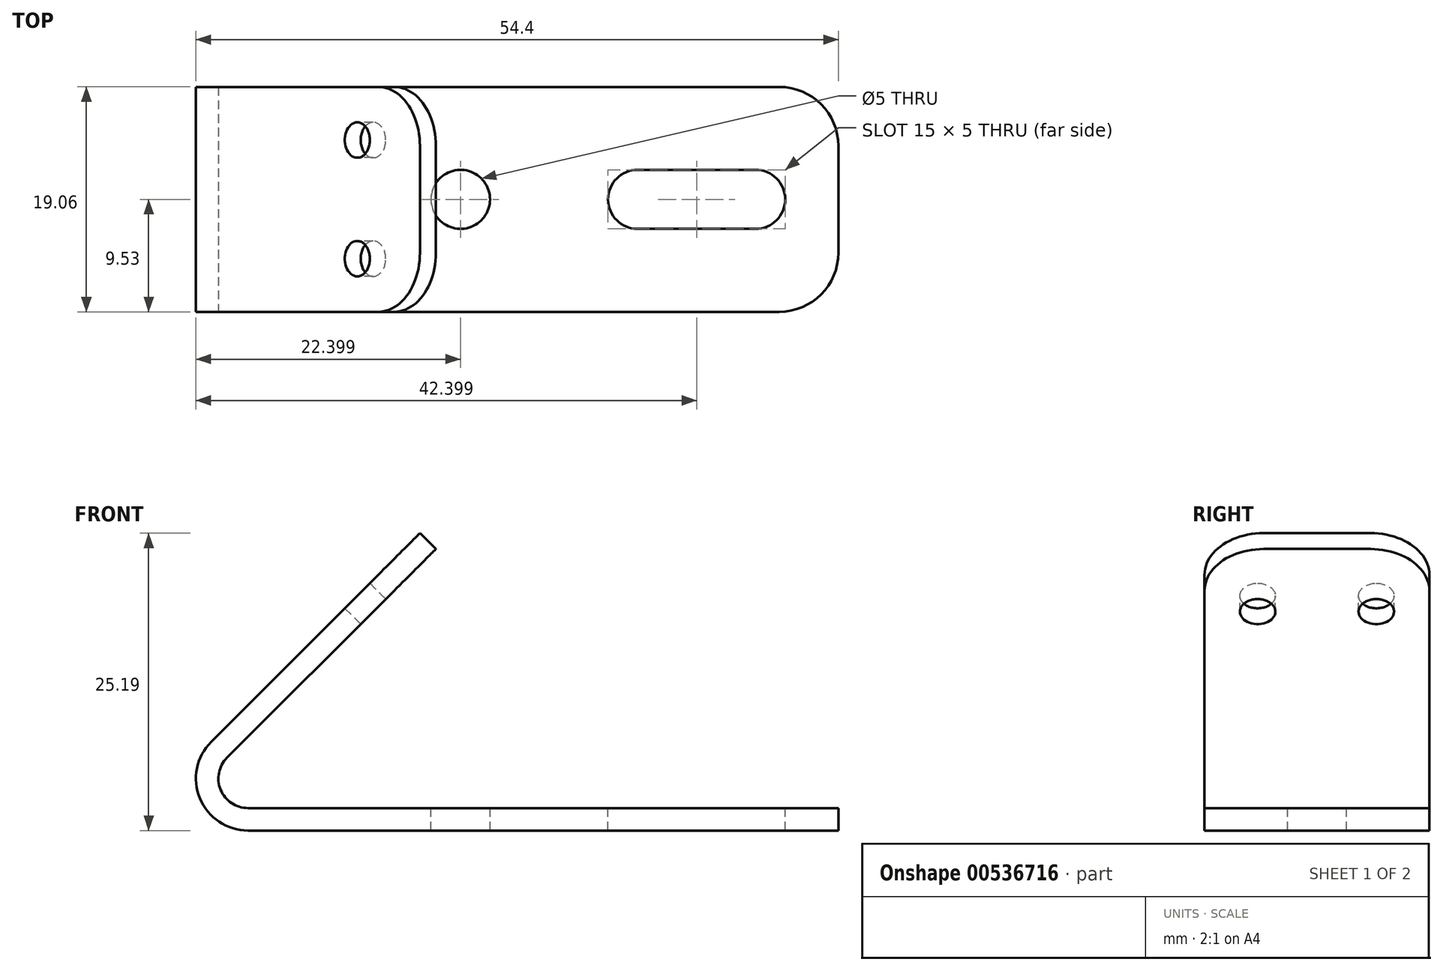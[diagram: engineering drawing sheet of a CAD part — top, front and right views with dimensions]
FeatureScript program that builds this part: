
annotation { "Feature Type Name" : "Feature", "Feature Type Description" : "" }
export const myFeature = defineFeature(function(context is Context, id is Id, definition is map)
    precondition{}
    {
        {
            var Q0;
            Q0=qCreatedBy(makeId("Front.planeOp"),FACE);
            var sketch = newSketch(context, id + "F0", { "sketchPlane" : qUnion([Q0])});
            skLineSegment(sketch, "E0", {"start": v(4.38, -27.35) * mm, "end": v(-45.62, -27.35) * mm});
            skLineSegment(sketch, "E1", {"start": v(-48.73, -19.84) * mm, "end": v(-31.06, -2.16) * mm});
            skLineSegment(sketch, "E2", {"start": v(-29.71, -3.5) * mm, "end": v(-47.39, -21.18) * mm});
            skLineSegment(sketch, "E3", {"start": v(-45.62, -25.45) * mm, "end": v(4.38, -25.45) * mm});
            skLineSegment(sketch, "E4", {"start": v(4.38, -25.45) * mm, "end": v(4.38, -27.35) * mm});
            skPoint(sketch, "E5.visualSharp", {"position": v(-56.24, -27.35) * mm});
            skArc(sketch, "E5.filletArc", {"start": v(-48.73, -19.84) * mm, "mid": v(-49.69, -24.63) * mm, "end": v(-45.62, -27.35) * mm});
            skLineSegment(sketch, "E6", {"start": v(-31.06, -2.16) * mm, "end": v(-29.71, -3.5) * mm});
            skPoint(sketch, "E7.visualSharp", {"position": v(-51.66, -25.45) * mm});
            skArc(sketch, "E7.filletArc", {"start": v(-47.39, -21.18) * mm, "mid": v(-47.93, -23.9) * mm, "end": v(-45.62, -25.45) * mm});
            skSolve(sketch);
        }
        {
            var Q0;
            Q0 = qSketchRegion(id + "F0", true);
            extrude(context, id + "F1", {"entities" : qUnion([Q0]), "endBound" : BoundingType.SYMMETRIC, "oppositeDirection" : true, "depth" : 19.05 * mm, "offsetDistance" : 25 * mm});
        }
        {
            var Q0;
            Q0=makeQuery(id+"F1.opExtrude","SWEPT_FACE",FACE,{"disambiguationData":[OSD([sQuery(id+"F0.wireOp",EDGE,"E1")])]});
            var sketch = newSketch(context, id + "F2", { "sketchPlane" : qUnion([Q0])});
            skLineSegment(sketch, "E8", {"start": v(-9.53, -23.49) * mm, "end": v(9.52, -23.49) * mm});
            skLineSegment(sketch, "E9", {"start": v(-9.53, -48.49) * mm, "end": v(-9.53, -23.49) * mm});
            skLineSegment(sketch, "E10", {"start": v(-9.53, -48.49) * mm, "end": v(9.52, -48.49) * mm});
            skLineSegment(sketch, "E11", {"start": v(9.53, -48.49) * mm, "end": v(9.53, -23.49) * mm});
            skCircle(sketch, "E12", {"center": v(-5.03, -30.99) * mm, "radius": 1.5 * mm});
            skCircle(sketch, "E13", {"center": v(5.03, -30.99) * mm, "radius": 1.5 * mm});
            skSolve(sketch);
        }
        {
            var Q0;
            Q0=makeQuery(id+"F2.imprint","IMPRINT",FACE,{"disambiguationData":[TD([[makeQuery(id+"F2.imprint","IMPRINT",EDGE,{"derivedFrom":sQuery(id+"F2.wireOp",EDGE,"E12")}),1.0]])]});
            var Q1;
            Q1=makeQuery(id+"F2.imprint","IMPRINT",FACE,{"disambiguationData":[TD([[makeQuery(id+"F2.imprint","IMPRINT",EDGE,{"derivedFrom":sQuery(id+"F2.wireOp",EDGE,"E13")}),1.0]])]});
            var Q2;
            Q2=sQuery(id+"F2.wireOp",EDGE,"E12");
            var Q3;
            Q3=sQuery(id+"F2.wireOp",EDGE,"E13");
            var Q4;
            Q4=makeQuery(id+"F1.opExtrude","SWEPT_FACE",FACE,{"disambiguationData":[OSD([sQuery(id+"F0.wireOp",EDGE,"E2")])]});
            extrude(context, id + "F3", {"entities" : qUnion([Q0, Q1]), "operationType" : NewBodyOperationType.REMOVE, "surfaceEntities" : qUnion([Q2, Q3]), "endBound" : BoundingType.UP_TO_SURFACE, "oppositeDirection" : true, "depth" : 25 * mm, "endBoundEntityFace" : qUnion([Q4]), "offsetDistance" : 25 * mm});
        }
        {
            var Q0;
            Q0=makeQuery(id+"F1.opExtrude","SWEPT_FACE",FACE,{"disambiguationData":[OSD([sQuery(id+"F0.wireOp",EDGE,"E3")])]});
            var sketch = newSketch(context, id + "F4", { "sketchPlane" : qUnion([Q0])});
            skPoint(sketch, "E14.0", {"position": v(4.38, 9.53) * mm});
            skPoint(sketch, "E15.0", {"position": v(4.38, -9.53) * mm});
            skPoint(sketch, "E16.0", {"position": v(-29.71, 9.53) * mm});
            skPoint(sketch, "E17.0", {"position": v(-29.71, -9.53) * mm});
            skCircle(sketch, "E18", {"center": v(-27.62, 0) * mm, "radius": 2.5 * mm});
            skArc(sketch, "E19", {"start": v(-12.62, 2.5) * mm, "mid": v(-15.12, 0) * mm, "end": v(-12.62, -2.5) * mm});
            skArc(sketch, "E20", {"start": v(-2.62, -2.5) * mm, "mid": v(-0.12, 0) * mm, "end": v(-2.62, 2.5) * mm});
            skLineSegment(sketch, "E21", {"start": v(-12.62, 2.5) * mm, "end": v(-2.62, 2.5) * mm});
            skLineSegment(sketch, "E22", {"start": v(-12.62, -2.5) * mm, "end": v(-2.62, -2.5) * mm});
            skSolve(sketch);
        }
        {
            var Q0;
            Q0 = qSketchRegion(id + "F4", true);
            var Q1;
            Q1=makeQuery(id+"F1.opExtrude","SWEPT_FACE",FACE,{"disambiguationData":[OSD([sQuery(id+"F0.wireOp",EDGE,"E0")])]});
            extrude(context, id + "F5", {"entities" : qUnion([Q0]), "operationType" : NewBodyOperationType.REMOVE, "endBound" : BoundingType.UP_TO_SURFACE, "oppositeDirection" : true, "depth" : 25 * mm, "endBoundEntityFace" : qUnion([Q1]), "offsetDistance" : 25 * mm});
        }
        {
            var Q0;
            Q0=makeQuery(id+"F1.opExtrude","CAP_EDGE",EDGE,{"disambiguationData":[OSD([sQuery(id+"F0.wireOp",EDGE,"E4")])],"isStart":true});
            var Q1;
            Q1=makeQuery(id+"F1.opExtrude","CAP_EDGE",EDGE,{"disambiguationData":[OSD([sQuery(id+"F0.wireOp",EDGE,"E4")])],"isStart":false});
            var Q2;
            Q2=makeQuery(id+"F1.opExtrude","CAP_EDGE",EDGE,{"disambiguationData":[OSD([sQuery(id+"F0.wireOp",EDGE,"E6")])],"isStart":false});
            var Q3;
            Q3=makeQuery(id+"F1.opExtrude","CAP_EDGE",EDGE,{"disambiguationData":[OSD([sQuery(id+"F0.wireOp",EDGE,"E6")])],"isStart":true});
            fillet(context, id + "F6", {"entities" : qUnion([Q0, Q1, Q2, Q3]), "radius" : 5 * mm, "tangentPropagation" : true, "allowEdgeOverflow" : false});
        }
    });
